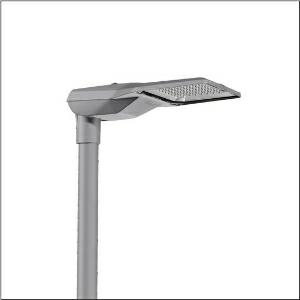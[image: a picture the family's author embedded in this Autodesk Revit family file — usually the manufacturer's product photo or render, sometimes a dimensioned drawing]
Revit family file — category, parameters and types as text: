
# Revit family: streetlight_sl_21_midi___st1_0a_5xe3d43s08lb_ab8b
name_source: partatom
category: Lighting Fixtures
units: mm (PartAtom-declared; Revit-internal decimal feet)

## family parameters
Cut with Voids When Loaded = No
Host = Face
Light Source = No
Part Type = Normal
Room Calculation Point = No
Round Connector Dimension = Use Diameter
Shared = No

## types (1)
- --- (1 x LED, 14950 lm, 99.6 W, 4000K)
    Apparent Load = 100 VA
    CIE Flux Codes = 37 72 97 100 100
    Color Rendering = 70
    Color Temperature = 4000K
    Default Elevation = 1800 mm
    Description = Streetlight SL 21 midi, mast luminaire, primary light control with lens, of PMMA, primary optical cover: cover, of toughened safety glass, transparent, light distribution: ST1.0a, light emission: direct distribution, primary light characteristic: asymmetric, installation type: side-entry, post-top, LED, High Power LED, rated luminous flux: 14.950lm, luminous efficacy: 150lm/W, light colour: 740, colour temperature: 4000K, control gear: D4i, control: overheat protection, constant luminous flux control, time-dependent luminous flux control, flexible luminous flux parameterisation, pre-setting: logarithmic dimming characteristic, mains connection: 230..240V, AC, 50/60Hz, start of lifetime: 100W, end of service life: 102W, reduction: 46W, luminaire housing, of diecast aluminium, powder-coated, SITECO metallic grey (DB 702S), corrosivity category C5 high according to DIN EN ISO 12944, please order mast flange separately, inclination adjustable: 0°, 5°, 10°, 15°, sealing non-destructively replaceable, multi-level sealing system, length: 644mm, width: 335mm, height: 110mm, mast flange for spigot size: 42mm (side-entry): 5XC10008XM4, 60/48mm (side-entry/post-top): 5XC10108XM2, 76/60mm (side-entry/post-top): 5XC10108XM1, mounting height: 4..8m, Smart Interface above, protection rating (complete): IP66, insulation class (complete): insulation class II (safety insulation), certification: CE, ENEC, ENEC+, VDE, impact resistance: IK10, permissible operating ambient temperature for outdoor applications: -40..+50°C, standard-compliant lighting for roads and squares, packaging unit: 1 piece

Light Distribution: ST1.0a
    Height = 111 mm
    Lamp = 1 x LED
    Lamp Light Flux = 14950 lm
    Lamp Power = 99.6 W
    Lamp count = 1
    Length = 644 mm
    Luminous efficacy = 150 lm/W
    Manufacturer = Siteco
    ModVariant = No
    Model = 5XE3D43S08LB
    Number of Poles = 1
    OnlyDefault = Yes
    Power Factor = 1
    Product Name = Streetlight SL 21 midi | ST1.0a
    Product group = mast luminaire | pylon top
    ProductGroupID = 6100
    Protection Class = Protection class II
    Protection Degree = IP 66
    RLX_Detail_Level = 1
    RLX_Emergency_Light_Flux = 0 lm
    RLX_Emergency_Type = 0
    RLX_Emergency_Type_DB = No
    RlxData = <blob elided: 26801 chars, md5=857d691d>
    Socket = socket
    Standby Power = 0 W
    System Light Flux = 14950 lm
    System Power = 100 W
    Type Comments = factory setting: luminous flux: 100 % | dim-lin: 254 | 1020 mA
    Type Image = l_1004302.jpg
    URL = http://relux.com
    VarID = @adj_031881
    Voltage = 0 V
    Weight = 0.00 kg
    Width = 336 mm

## geometry (parser evidence)
native form markers: Blend x4, Sweep x12
no freeform markers — native parametric forms only
